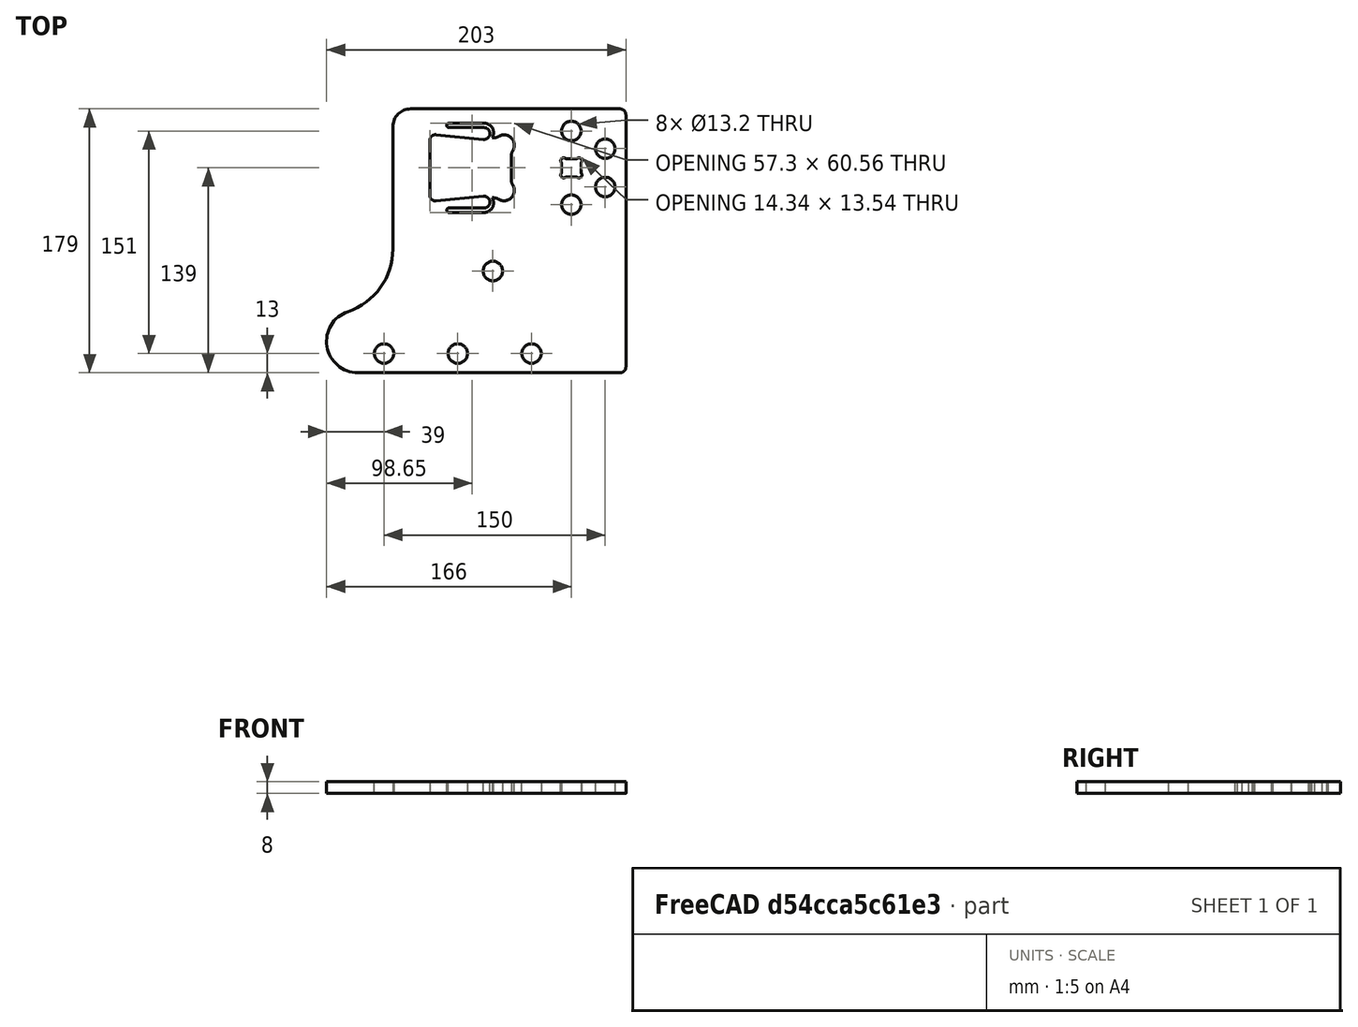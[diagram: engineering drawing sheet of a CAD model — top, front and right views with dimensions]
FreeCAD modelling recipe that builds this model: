
FCSTD DOCUMENT  (FreeCAD 0.19R24267 +99 (Git))
Label: V2 Tabbed end plate opposing plate
License: All rights reserved
LicenseURL: http://en.wikipedia.org/wiki/All_rights_reserved
objects: Sketcher::SketchObject×1, PartDesign::Pad×1, PartDesign::Body×1
note: 4 computed .brp shape members not serialized (recipe doc carries the construction recipe); baked Part::Feature solids carry a one-line shape summary decoded from their .brp

FEATURE [Sketcher::SketchObject] Sketch
  FullyConstrained = true
  MapMode = 5
  Support = -> [XY_Plane]
  sketch-geometry (84):
    g0: Circle CenterX=-37 CenterY=25 CenterZ=0 NormalX=0 NormalY=0 NormalZ=1 AngleXU=0 Radius=6.6
    g1: Circle CenterX=-37 CenterY=-25 CenterZ=0 NormalX=0 NormalY=0 NormalZ=1 AngleXU=0 Radius=6.6
    g2: LineSegment StartX=-37 StartY=25 StartZ=0 EndX=-37 EndY=-25 EndZ=0
    g3: GeomPoint X=-37 Y=0 Z=0
    g4: LineSegment StartX=-40.1018 StartY=6.2 StartZ=0 EndX=-33.8982 EndY=6.2 EndZ=0
    g5: LineSegment StartX=-30.4 StartY=2.70176 StartZ=0 EndX=-30.4 EndY=-2.70176 EndZ=0
    g6: LineSegment StartX=-33.8982 StartY=-6.2 StartZ=0 EndX=-40.1018 EndY=-6.2 EndZ=0
    g7: LineSegment StartX=-43.6 StartY=-2.70176 StartZ=0 EndX=-43.6 EndY=2.70176 EndZ=0
    g8: Circle CenterX=-14 CenterY=13 CenterZ=0 NormalX=0 NormalY=0 NormalZ=1 AngleXU=0 Radius=6.6
    g9: Circle CenterX=-14 CenterY=-13 CenterZ=0 NormalX=0 NormalY=0 NormalZ=1 AngleXU=0 Radius=6.6
    g10: LineSegment StartX=-14 StartY=13 StartZ=0 EndX=-14 EndY=-13 EndZ=0
    g11: ArcOfCircle CenterX=-42.1858 CenterY=4.78579 CenterZ=0 NormalX=0 NormalY=0 NormalZ=1 AngleXU=0 Radius=2 StartAngle=1.02277 EndAngle=3.68962
    g12: ArcOfCircle CenterX=-31.8142 CenterY=4.78579 CenterZ=0 NormalX=0 NormalY=0 NormalZ=1 AngleXU=0 Radius=2 StartAngle=5.73516 EndAngle=8.40201
    g13: ArcOfCircle CenterX=-31.8142 CenterY=-4.78579 CenterZ=0 NormalX=0 NormalY=0 NormalZ=1 AngleXU=0 Radius=2 StartAngle=4.16436 EndAngle=6.83121
    g14: ArcOfCircle CenterX=-42.1858 CenterY=-4.78579 CenterZ=0 NormalX=0 NormalY=0 NormalZ=1 AngleXU=0 Radius=2 StartAngle=2.59356 EndAngle=5.26042
    g15: LineSegment StartX=-43.6 StartY=2.70176 StartZ=0 EndX=-43.6 EndY=6.2 EndZ=0
    g16: LineSegment StartX=-40.1018 StartY=6.2 StartZ=0 EndX=-43.6 EndY=6.2 EndZ=0
    g17: LineSegment StartX=-33.8982 StartY=6.2 StartZ=0 EndX=-30.4 EndY=6.2 EndZ=0
    g18: LineSegment StartX=-30.4 StartY=2.70176 StartZ=0 EndX=-30.4 EndY=6.2 EndZ=0
    g19: LineSegment StartX=-30.4 StartY=-2.70176 StartZ=0 EndX=-30.4 EndY=-6.2 EndZ=0
    g20: LineSegment StartX=-33.8982 StartY=-6.2 StartZ=0 EndX=-30.4 EndY=-6.2 EndZ=0
    g21: LineSegment StartX=-40.1018 StartY=-6.2 StartZ=0 EndX=-43.6 EndY=-6.2 EndZ=0
    g22: LineSegment StartX=-43.6 StartY=-2.70176 StartZ=0 EndX=-43.6 EndY=-6.2 EndZ=0
    g23: ArcOfCircle CenterX=-40.1018 CenterY=8.2 CenterZ=0 NormalX=0 NormalY=0 NormalZ=1 AngleXU=0 Radius=2 StartAngle=4.16436 EndAngle=4.71239
    g24: ArcOfCircle CenterX=-45.6 CenterY=2.70176 CenterZ=0 NormalX=0 NormalY=0 NormalZ=1 AngleXU=0 Radius=2 StartAngle=1e-16 EndAngle=0.548028
    g25: ArcOfCircle CenterX=-33.8982 CenterY=8.2 CenterZ=0 NormalX=0 NormalY=0 NormalZ=1 AngleXU=0 Radius=2 StartAngle=4.71239 EndAngle=5.26042
    g26: ArcOfCircle CenterX=-28.4 CenterY=2.70176 CenterZ=0 NormalX=0 NormalY=0 NormalZ=1 AngleXU=0 Radius=2 StartAngle=2.59356 EndAngle=3.14159
    g27: ArcOfCircle CenterX=-45.6 CenterY=-2.70176 CenterZ=0 NormalX=0 NormalY=0 NormalZ=1 AngleXU=0 Radius=2 StartAngle=5.73516 EndAngle=6.28319
    g28: ArcOfCircle CenterX=-40.1018 CenterY=-8.2 CenterZ=0 NormalX=0 NormalY=0 NormalZ=1 AngleXU=0 Radius=2 StartAngle=1.5708 EndAngle=2.11882
    g29: ArcOfCircle CenterX=-33.8982 CenterY=-8.2 CenterZ=0 NormalX=0 NormalY=0 NormalZ=1 AngleXU=0 Radius=2 StartAngle=1.02277 EndAngle=1.5708
    g30: ArcOfCircle CenterX=-28.4 CenterY=-2.70176 CenterZ=0 NormalX=0 NormalY=0 NormalZ=1 AngleXU=0 Radius=2 StartAngle=3.14159 EndAngle=3.68962
    g31: LineSegment StartX=-4 StartY=40 StartZ=0 EndX=-146 EndY=40 EndZ=0
    g32: LineSegment StartX=-102.7 StartY=20.3 StartZ=0 EndX=-102.7 EndY=-20.3 EndZ=0
    g33: ArcOfCircle CenterX=-4 CenterY=36 CenterZ=0 NormalX=0 NormalY=0 NormalZ=1 AngleXU=0 Radius=4 StartAngle=0 EndAngle=1.5708
    g34: LineSegment StartX=-96.2 StartY=20.3 StartZ=0 EndX=-96.2 EndY=-20.3 EndZ=0
    g35: LineSegment StartX=-90.7 StartY=20.3 StartZ=0 EndX=-90.7 EndY=-20.3 EndZ=0
    g36: LineSegment StartX=-90.7 StartY=20.3 StartZ=0 EndX=-89.9438 EndY=20.3 EndZ=0
    g37: LineSegment StartX=-90.7 StartY=-20.3 StartZ=0 EndX=-89.9438 EndY=-20.3 EndZ=0
    g38: LineSegment StartX=-77.7 StartY=8.05618 StartZ=0 EndX=-77.7 EndY=-8.05618 EndZ=0
    g39: ArcOfCircle CenterX=-82.6497 CenterY=15.3503 CenterZ=0 NormalX=0 NormalY=0 NormalZ=1 AngleXU=0 Radius=7 StartAngle=5.73516 EndAngle=8.40201
    g40: ArcOfCircle CenterX=-82.6497 CenterY=-15.3503 CenterZ=0 NormalX=0 NormalY=0 NormalZ=1 AngleXU=0 Radius=7 StartAngle=4.16436 EndAngle=6.83121
    g41: ArcOfCircle CenterX=-89.9438 CenterY=-27.3 CenterZ=0 NormalX=0 NormalY=0 NormalZ=1 AngleXU=0 Radius=7 StartAngle=1.02277 EndAngle=1.5708
    g42: ArcOfCircle CenterX=-70.7 CenterY=-8.05618 CenterZ=0 NormalX=0 NormalY=0 NormalZ=1 AngleXU=0 Radius=7 StartAngle=3.14159 EndAngle=3.68962
    g43: ArcOfCircle CenterX=-70.7 CenterY=8.05618 CenterZ=0 NormalX=0 NormalY=0 NormalZ=1 AngleXU=0 Radius=7 StartAngle=2.59356 EndAngle=3.14159
    g44: ArcOfCircle CenterX=-89.9438 CenterY=27.3 CenterZ=0 NormalX=0 NormalY=0 NormalZ=1 AngleXU=0 Radius=7 StartAngle=4.71239 EndAngle=5.26042
    g45: LineSegment StartX=-89.9438 StartY=20.3 StartZ=0 EndX=-77.7 EndY=20.3 EndZ=0
    g46: LineSegment StartX=-77.7 StartY=8.05618 StartZ=0 EndX=-77.7 EndY=20.3 EndZ=0
    g47: LineSegment StartX=-89.9438 StartY=-20.3 StartZ=0 EndX=-77.7 EndY=-20.3 EndZ=0
    g48: LineSegment StartX=-77.7 StartY=-8.05618 StartZ=0 EndX=-77.7 EndY=-20.3 EndZ=0
    g49: Circle CenterX=-164 CenterY=-126 CenterZ=0 NormalX=0 NormalY=0 NormalZ=1 AngleXU=0 Radius=6.6
    g50: Circle CenterX=-114 CenterY=-126 CenterZ=0 NormalX=0 NormalY=0 NormalZ=1 AngleXU=0 Radius=6.6
    g51: Circle CenterX=-64 CenterY=-126 CenterZ=0 NormalX=0 NormalY=0 NormalZ=1 AngleXU=0 Radius=6.6
    g52: LineSegment StartX=-164 StartY=-126 StartZ=0 EndX=-114 EndY=-126 EndZ=0
    g53: LineSegment StartX=-114 StartY=-126 StartZ=0 EndX=-64 EndY=-126 EndZ=0
    g54: LineSegment StartX=-181.75 StartY=-139 StartZ=0 EndX=-4 EndY=-139 EndZ=0
    g55: LineSegment StartX=0 StartY=36 StartZ=0 EndX=0 EndY=-135 EndZ=0
    g56: ArcOfCircle CenterX=-4 CenterY=-135 CenterZ=0 NormalX=0 NormalY=0 NormalZ=1 AngleXU=0 Radius=4 StartAngle=4.71239 EndAngle=6.28319
    g57: ArcOfCircle CenterX=-203 CenterY=-55 CenterZ=0 NormalX=0 NormalY=0 NormalZ=1 AngleXU=0 Radius=45 StartAngle=5.03892 EndAngle=6.28319
    g58: LineSegment StartX=-158 StartY=-55 StartZ=0 EndX=-158 EndY=28 EndZ=0
    g59: Circle CenterX=-90.2 CenterY=-70 CenterZ=0 NormalX=0 NormalY=0 NormalZ=1 AngleXU=0 Radius=6.6
    g60: ArcOfCircle CenterX=-146 CenterY=28 CenterZ=0 NormalX=0 NormalY=0 NormalZ=1 AngleXU=0 Radius=12 StartAngle=1.5708 EndAngle=3.14159
    g61: LineSegment StartX=-90.7 StartY=20.3 StartZ=0 EndX=-158 EndY=20.3 EndZ=0
    g62: LineSegment StartX=-90.7 StartY=-20.3 StartZ=0 EndX=-158 EndY=-20.3 EndZ=0
    g63: LineSegment StartX=-133 StartY=18.5247 StartZ=0 EndX=-133 EndY=-18.5247 EndZ=0
    g64: LineSegment StartX=-128.601 StartY=22.5048 StartZ=0 EndX=-96.5986 EndY=19.3 EndZ=0
    g65: LineSegment StartX=-128.601 StartY=-22.5048 StartZ=0 EndX=-96.5986 EndY=-19.3 EndZ=0
    g66: GeomPoint X=-106.584 Y=20.3 Z=0
    g67: GeomPoint X=-106.584 Y=-20.3 Z=0
    g68: ArcOfCircle CenterX=-129 CenterY=18.5247 CenterZ=0 NormalX=0 NormalY=0 NormalZ=1 AngleXU=0 Radius=4 StartAngle=1.47099 EndAngle=3.14159
    g69: ArcOfCircle CenterX=-129 CenterY=-18.5247 CenterZ=0 NormalX=0 NormalY=0 NormalZ=1 AngleXU=0 Radius=4 StartAngle=3.14159 EndAngle=4.8122
    g70: GeomPoint X=-132.584 Y=20.3 Z=0
    g71: LineSegment StartX=-96.2 StartY=20.3 StartZ=0 EndX=-96.2 EndY=23.2801 EndZ=0
    g72: ArcOfCircle CenterX=-96.2 CenterY=23.2801 CenterZ=0 NormalX=0 NormalY=0 NormalZ=1 AngleXU=0 Radius=4 StartAngle=4.61258 EndAngle=7.85398
    g73: ArcOfCircle CenterX=-96.2 CenterY=-23.2801 CenterZ=0 NormalX=0 NormalY=0 NormalZ=1 AngleXU=0 Radius=4 StartAngle=4.71239 EndAngle=7.95379
    g74: LineSegment StartX=-96.2 StartY=27.2801 StartZ=0 EndX=-120 EndY=27.2801 EndZ=0
    g75: LineSegment StartX=-96.2 StartY=-27.2801 StartZ=0 EndX=-120 EndY=-27.2801 EndZ=0
    g76: LineSegment StartX=-96.2 StartY=30.2801 StartZ=0 EndX=-120 EndY=30.2801 EndZ=0
    g77: LineSegment StartX=-96.2 StartY=-30.2801 StartZ=0 EndX=-120 EndY=-30.2801 EndZ=0
    g78: ArcOfCircle CenterX=-120 CenterY=28.7801 CenterZ=0 NormalX=0 NormalY=0 NormalZ=1 AngleXU=0 Radius=1.5 StartAngle=1.5708 EndAngle=4.71239
    g79: ArcOfCircle CenterX=-120 CenterY=-28.7801 CenterZ=0 NormalX=0 NormalY=0 NormalZ=1 AngleXU=0 Radius=1.5 StartAngle=1.5708 EndAngle=4.71239
    g80: ArcOfCircle CenterX=-96.2 CenterY=-23.7745 CenterZ=0 NormalX=0 NormalY=0 NormalZ=1 AngleXU=0 Radius=6.50556 StartAngle=4.71239 EndAngle=6.84661
    g81: ArcOfCircle CenterX=-96.2 CenterY=23.7745 CenterZ=0 NormalX=0 NormalY=0 NormalZ=1 AngleXU=0 Radius=6.50556 StartAngle=5.71976 EndAngle=7.85398
    g82: ArcOfCircle CenterX=-181.75 CenterY=-117.75 CenterZ=0 NormalX=0 NormalY=0 NormalZ=1 AngleXU=0 Radius=21.2503 StartAngle=1.89733 EndAngle=4.71239
    g83: LineSegment StartX=-203 StartY=-55 StartZ=0 EndX=-203 EndY=-117.75 EndZ=0
  constraints (214):
    c: Symmetric(g0,g1,g-1)
    c: DistanceY(g1,g0) = 50
    c: Coincident(g2,g0)
    c: Coincident(g2,g1)
    c: Equal(g1,g0)
    c: PointOnObject(g3,g2)
    c: PointOnObject(g3,g-1)
    c: Horizontal(g4)
    c: Horizontal(g6)
    c: Vertical(g5)
    c: Vertical(g7)
    c: Coincident(g10,g8)
    c: Coincident(g10,g9)
    c: Equal(g9,g8)
    c: Equal(g8,g0)
    c: DistanceY(g10,g10) = 26
    c: Symmetric(g8,g9,g-1)
    c: Equal(g11,g12)
    c: Equal(g12,g13)
    c: Equal(g13,g14)
    c: PointOnObject(g15,g11)
    c: Coincident(g16,g15)
    c: PointOnObject(g17,g12)
    c: Coincident(g18,g17)
    c: PointOnObject(g19,g13)
    c: Coincident(g20,g19)
    c: PointOnObject(g21,g14)
    c: Coincident(g22,g21)
    c: Equal(g22,g21)
    c: Equal(g21,g20)
    c: Equal(g20,g19)
    c: Equal(g19,g18)
    c: Equal(g18,g17)
    c: Equal(g17,g16)
    c: Equal(g16,g15)
    c: Vertical(g15)
    c: Vertical(g22)
    c: Vertical(g19)
    c: Vertical(g18)
    c: Horizontal(g16)
    c: Tangent(g11,g23) = 1.5708
    c: Tangent(g4,g23) = -1.5708
    c: Tangent(g11,g24) = 1.5708
    c: Tangent(g7,g24) = -1.5708
    c: Tangent(g12,g25) = 1.5708
    c: Tangent(g4,g25) = -1.5708
    c: Tangent(g12,g26) = 1.5708
    c: Tangent(g5,g26) = -1.5708
    c: Tangent(g14,g27) = 1.5708
    c: Tangent(g7,g27) = -1.5708
    c: Tangent(g14,g28) = 1.5708
    c: Tangent(g6,g28) = -1.5708
    c: Tangent(g13,g29) = 1.5708
    c: Tangent(g6,g29) = -1.5708
    c: Tangent(g13,g30) = 1.5708
    c: Tangent(g5,g30) = -1.5708
    c: Coincident(g5,g19)
    c: Coincident(g6,g20)
    c: Coincident(g6,g21)
    c: Coincident(g7,g22)
    c: Coincident(g7,g15)
    c: Coincident(g18,g5)
    c: Coincident(g4,g16)
    c: Coincident(g4,g17)
    c: Horizontal(g21)
    c: Horizontal(g17)
    c: Horizontal(g20)
    c: Equal(g23,g24)
    c: Equal(g24,g11)
    c: Equal(g27,g28)
    c: Equal(g12,g25)
    c: Equal(g13,g30)
    c: DistanceX(g21,g19) = 13.2
    c: DistanceY(g19,g17) = 12.4
    c: Radius(g12) = 2
    c: Symmetric(g21,g17,g3)
    c: DistanceX(g8,g-1) = 14
    c: Horizontal(g31)
    c: Vertical(g32)
    c: Tangent(g31,g33) = -1.5708
    c: Radius(g33) = 4
    c: DistanceX(g32,g34) = 6.5
    c: Symmetric(g34,g34,g-1)
    c: Symmetric(g35,g35,g-1)
    c: DistanceX(g32,g35) = 12
    c: Coincident(g36,g35)
    c: Horizontal(g36)
    c: Coincident(g37,g35)
    c: Horizontal(g37)
    c: Vertical(g38)
    c: Tangent(g40,g41) = 1.5708
    c: Tangent(g37,g41) = 1.5708
    c: Tangent(g40,g42) = 1.5708
    c: Tangent(g38,g42) = -1.5708
    c: Tangent(g39,g43) = 1.5708
    c: Tangent(g38,g43) = -1.5708
    c: Tangent(g39,g44) = 1.5708
    c: Tangent(g36,g44) = -1.5708
    c: Coincident(g45,g36)
    c: PointOnObject(g45,g39)
    c: Coincident(g46,g38)
    c: Coincident(g46,g45)
    c: Tangent(g46,g43)
    c: Coincident(g47,g37)
    c: PointOnObject(g47,g40)
    c: Tangent(g47,g41)
    c: Coincident(g48,g38)
    c: Coincident(g48,g47)
    c: Vertical(g48)
    c: Equal(g44,g43)
    c: Equal(g43,g39)
    c: Horizontal(g45)
    c: Equal(g41,g40)
    c: Equal(g40,g42)
    c: Radius(g39) = 7
    c: DistanceX(g32,g38) = 25
    c: Equal(g48,g47)
    c: Equal(g47,g46)
    c: Equal(g46,g45)
    c: DistanceX(g1,g9) = 23
    c: DistanceX(g38,g1) = 40.7
    c: Coincident(g52,g49)
    c: Coincident(g52,g50)
    c: Horizontal(g52)
    c: Coincident(g53,g50)
    c: Coincident(g53,g51)
    c: Horizontal(g53)
    c: Equal(g49,g50)
    c: Equal(g50,g51)
    c: DistanceY(g49,g1) = 101
    c: Equal(g53,g52)
    c: DistanceX(g49,g51) = 100
    c: Horizontal(g54)
    c: Vertical(g55)
    c: Tangent(g55,g56) = 1.5708
    c: Tangent(g54,g56) = -1.5708
    c: Equal(g33,g56)
    c: DistanceY(g54,g51) = 13
    c: PointOnObject(g-1,g55)
    c: Tangent(g55,g33) = 1.5708
    c: DistanceX(g51,g1) = 27
    c: DistanceY(g57,g1) = 30
    c: DistanceX(g57,g1) = 166
    c: Vertical(g58)
    c: Radius(g57) = 45
    c: Tangent(g57,g58) = -1.5708
    c: Equal(g59,g51)
    c: DistanceY(g59,g-1) = 70
    c: Tangent(g31,g60) = -1.5708
    c: Tangent(g58,g60) = 1.5708
    c: Coincident(g61,g36)
    c: Horizontal(g61)
    c: Coincident(g62,g37)
    c: Horizontal(g62)
    c: PointOnObject(g61,g58)
    c: PointOnObject(g62,g58)
    c: PointOnObject(g34,g61)
    c: PointOnObject(g32,g61)
    c: PointOnObject(g32,g62)
    c: DistanceY(g62,g61) = 40.6
    c: Vertical(g63)
    c: PointOnObject(g66,g61)
    c: PointOnObject(g66,g64)
    c: PointOnObject(g67,g65)
    c: Symmetric(g66,g67,g-1)
    c: Tangent(g64,g68) = 1.5708
    c: Tangent(g63,g68) = -1.5708
    c: Tangent(g65,g69) = -1.5708
    c: Tangent(g63,g69) = -1.5708
    c: Equal(g68,g69)
    c: PointOnObject(g70,g61)
    c: PointOnObject(g70,g68)
    c: DistanceX(g70,g66) = 26
    c: DistanceX(g58,g63) = 25
    c: Radius(g68) = 4
    c: Radius(g60) = 12
    c: DistanceY(g-1,g31) = 40
    c: Coincident(g71,g34)
    c: Vertical(g71)
    c: Coincident(g72,g71)
    c: Symmetric(g71,g73,g-1)
    c: Radius(g72) = 4
    c: Horizontal(g74)
    c: Horizontal(g75)
    c: Tangent(g73,g75) = 1.5708
    c: Tangent(g65,g73) = 1.5708
    c: Tangent(g64,g72) = -1.5708
    c: DistanceY(g65,g64) = 38.6
    c: Tangent(g72,g74) = -1.5708
    c: Horizontal(g76)
    c: Horizontal(g77)
    c: Tangent(g79,g75) = -1.5708
    c: Tangent(g79,g77) = 1.5708
    c: Tangent(g78,g76) = -1.5708
    c: Tangent(g78,g74) = 1.5708
    c: Coincident(g80,g35)
    c: Tangent(g80,g77) = 1.5708
    c: Tangent(g81,g76) = -1.5708
    c: Symmetric(g79,g78,g-1)
    c: DistanceX(g58,g78) = 38
    c: Equal(g78,g79)
    c: Radius(g78) = 1.5
    c: Equal(g81,g80)
    c: Coincident(g36,g81)
    c: Equal(g74,g76)
    c: DistanceX(g59,g38) = 12.5
    c: Tangent(g82,g54) = -1.5708
    c: Tangent(g57,g82) = 1.5708
    c: Diameter(g51) = 13.2
    c: Equal(g51,g1)
    c: Coincident(g83,g57)
    c: PointOnObject(g83,g82)
    c: Vertical(g83)
    c: Tangent(g83,g82)
FEATURE [PartDesign::Pad] Pad  label="Plate thickness"
  Direction = (1,1,1)
  Length = 8
  Length2 = 100
  Profile = -> Sketch
  Reversed = true
  Type = 0
FEATURE [PartDesign::Body] Body
  Group = -> [Sketch,Pad]
  Origin = -> Origin
  Tip = -> Pad
